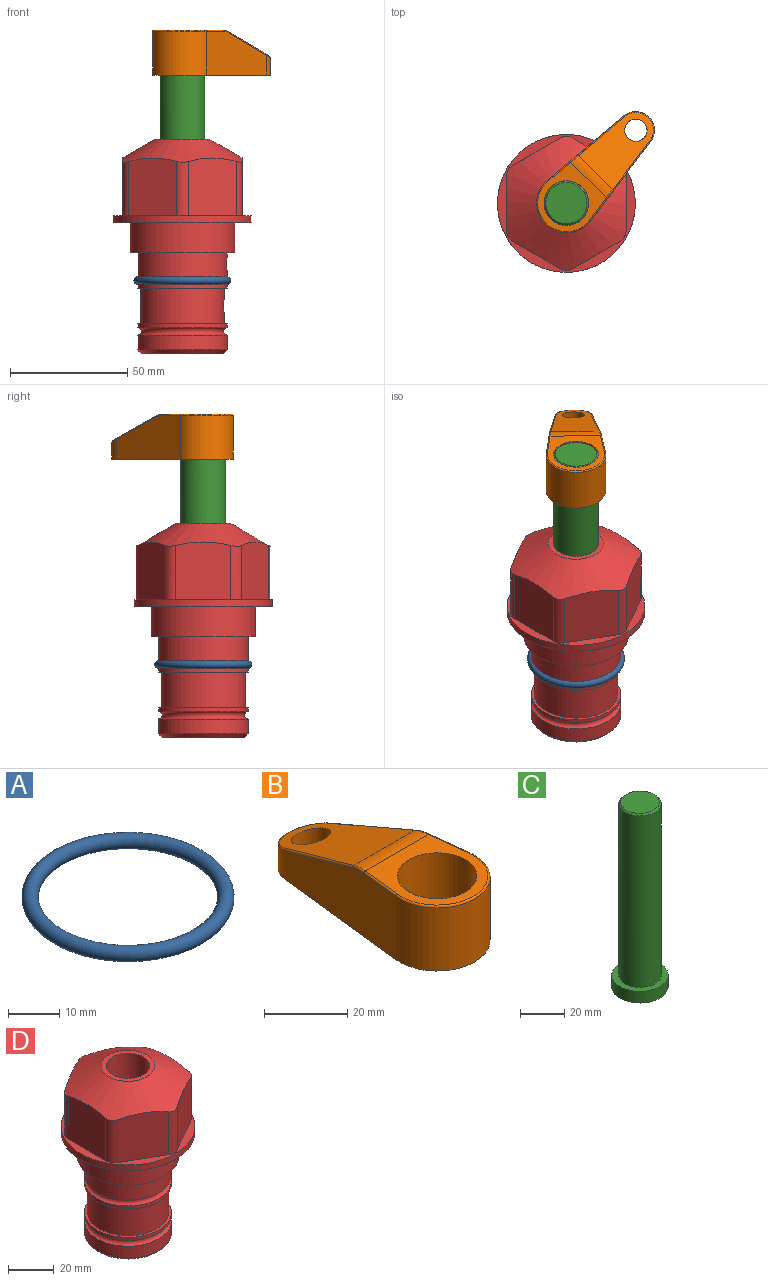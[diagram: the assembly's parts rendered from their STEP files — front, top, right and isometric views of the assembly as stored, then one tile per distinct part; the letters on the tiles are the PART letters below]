
ASSEMBLY  parts=4 mates=2
PART A: 1 faces, bbox 44.7x44.7x3.2 mm
  f0: torus R=19.05mm, axis (0,0,1), area 1193.9mm2
PART B: 44 faces, bbox 27.5x64.5x19.1 mm
  f0: plane 2.3x0.95mm, normal (0,0,-1), area 1mm2, adj f25,f30,f34
  f1: plane 63.5x25.4mm, normal (0,0,-1), area 561.7mm2, adj f2,f3,f4,f5,f6,f7,f19,f20
  f2: cylinder r=12.7mm len=25.4mm, axis (0,0,-1), area 792.2mm2, adj f1,f3,f5,f13
  f3: plane 42.33x18.54mm, normal (0.99,0.11,0), area 647mm2, adj f1,f2,f4,f11,f12,f14
  f4: cylinder r=7.94mm len=15.78mm, axis (0,0,-1), area 158.6mm2, adj f1,f3,f5,f16
  f5: plane 42.33x18.54mm, normal (-0.99,0.11,0), area 647mm2, adj f1,f2,f4,f15,f17,f18
  f6: cylinder r=9.53mm len=19.05mm, axis (0,0,-1), area 1140.1mm2, adj f1,f8
  f7: cylinder r=4.76mm len=10.98mm, axis (0,0,-1), area 276.1mm2, adj f1,f9
  f8: plane 25.83x24.38mm, normal (0,0,1), area 262.2mm2, adj f6,f10,f11,f13,f15
  f9: plane 32.49x20.55mm, normal (0,0.34,0.94), area 489.9mm2, adj f7,f10,f14,f16,f18
  f10: cylinder r=12.7mm len=21.49mm, axis (-1,0,0), area 93.2mm2, adj f8,f9,f12,f17
  f11: cylinder r=0.51mm len=12.34mm, axis (0.11,-0.99,0), area 9.9mm2, adj f3,f8,f12,f13
  f12: bspline ~7.62x1.64mm, area 3.5mm2, adj f3,f10,f11,f14
  f13: torus R=12.19mm, axis (0,0,1), area 33.6mm2, adj f2,f8,f11,f15
  f14: cylinder r=0.51mm len=26.01mm, axis (0.1,-0.93,0.34), area 21.6mm2, adj f3,f9,f12,f16
  f15: cylinder r=0.51mm len=12.34mm, axis (0.11,0.99,0), area 9.9mm2, adj f5,f8,f13,f17
  f16: bspline ~15.78x7.05mm, area 15.7mm2, adj f4,f9,f14,f18
  f17: bspline ~7.62x1.64mm, area 3.5mm2, adj f5,f10,f15,f18
  f18: cylinder r=0.51mm len=26.01mm, axis (0.1,0.93,-0.34), area 21.6mm2, adj f5,f9,f16,f17
  f19: plane 21.6x14.29mm, normal (-0.99,-0.11,0), area 242.6mm2, adj f1,f26,f28,f34,f36,f38
  f20: plane 21.6x14.29mm, normal (0.99,-0.11,0), area 242.6mm2, adj f1,f27,f29,f37,f39,f41
  f21: cylinder r=12.7mm len=14.29mm, axis (0,0,-1), area 173.2mm2, adj f1,f26,f27,f30,f31,f33
  f22: cylinder r=7.94mm len=7.63mm, axis (0,0,-1), area 53.8mm2, adj f1,f28,f29,f42
  f23: plane 2.3x0.95mm, normal (0,0,-1), area 1mm2, adj f25,f33,f37
  f24: plane 17.94x12.32mm, normal (0,-0.34,-0.94), area 191.2mm2, adj f25,f38,f41,f42
  f25: cylinder r=9.53mm len=12.93mm, axis (-1,0,0), area 37.5mm2, adj f0,f23,f24,f31,f36,f39
  f26: cylinder r=1.59mm len=14.29mm, axis (0,0,-1), area 49mm2, adj f1,f19,f21,f32
  f27: cylinder r=1.59mm len=14.29mm, axis (0,0,-1), area 49mm2, adj f1,f20,f21,f35
  f28: cylinder r=1.59mm len=7.28mm, axis (0,0,-1), area 22.1mm2, adj f1,f19,f22,f40
  f29: cylinder r=1.59mm len=7.28mm, axis (0,0,-1), area 22.1mm2, adj f1,f20,f22,f43
  f30: torus R=14.29mm, axis (0,0,1), area 5.8mm2, adj f0,f21,f31,f32
  f31: bspline ~11.06x2.73mm, area 20.8mm2, adj f21,f25,f30,f33
  f32: sphere r=1.59mm, area 5.4mm2, adj f26,f30,f34
  f33: torus R=14.29mm, axis (0,0,1), area 5.8mm2, adj f21,f23,f31,f35
  f34: cylinder r=1.59mm len=1.68mm, axis (-0.11,0.99,0), area 2.4mm2, adj f0,f19,f32,f36
  f35: sphere r=1.59mm, area 5.4mm2, adj f27,f33,f37
  f36: bspline ~5.82x2.33mm, area 7.7mm2, adj f19,f25,f34,f38
  f37: cylinder r=1.59mm len=1.68mm, axis (0.11,0.99,0), area 2.4mm2, adj f20,f23,f35,f39
  f38: cylinder r=1.59mm len=18.33mm, axis (0.1,-0.93,0.34), area 46.7mm2, adj f19,f24,f36,f40
  f39: bspline ~5.82x2.33mm, area 7.7mm2, adj f20,f25,f37,f41
  f40: sphere r=1.59mm, area 3.6mm2, adj f28,f38,f42
  f41: cylinder r=1.59mm len=18.33mm, axis (0.1,0.93,-0.34), area 46.7mm2, adj f20,f24,f39,f43
  f42: bspline ~8.31x1.84mm, area 15.3mm2, adj f22,f24,f40,f43
  f43: sphere r=1.59mm, area 3.6mm2, adj f29,f41,f42
PART C: 6 faces, bbox 25.4x25.4x101.6 mm
  f0: plane 17.46x17.46mm, normal (0,0,1), area 239.5mm2, adj f5
  f1: plane 25.4x25.4mm, normal (0,0,-1), area 506.7mm2, adj f2
  f2: cylinder r=12.7mm len=25.4mm, axis (0,0,1), area 506.7mm2, adj f1,f3
  f3: plane 25.4x25.4mm, normal (0,0,1), area 221.7mm2, adj f2,f4
  f4: cylinder r=9.53mm len=94.46mm, axis (0,0,1), area 5653mm2, adj f3,f5
  f5: cone r=8.73mm half-angle=45deg, axis (0,0,-1), area 64.4mm2, adj f0,f4
PART D: 36 faces, bbox 58.7x58.7x91.2 mm
  f0: cylinder r=17.78mm len=35.56mm, axis (0,0,1), area 1670.8mm2, adj f23,f24,f31
  f1: cylinder r=19.05mm len=38.1mm, axis (0,0,1), area 1191.9mm2, adj f26,f27,f30
  f2: plane 58.66x58.66mm, normal (0,0,-1), area 1150.6mm2, adj f3,f28
  f3: cylinder r=29.33mm len=58.66mm, axis (0,0,-1), area 585.1mm2, adj f2,f4
  f4: plane 58.66x58.66mm, normal (0,0,1), area 475.9mm2, adj f3,f5,f6,f7,f8,f9,f10,f11
  f5: plane 24.5x20.32mm, normal (0.5,-0.87,0), area 562.8mm2, adj f4,f15,f16,f17
  f6: plane 24.5x20.32mm, normal (-0.5,-0.87,0), area 562.8mm2, adj f4,f14,f15,f17
  f7: plane 24.5x23.48mm, normal (-1,0,0), area 562.8mm2, adj f4,f13,f14,f17
  f8: plane 24.5x20.32mm, normal (-0.5,0.87,0), area 562.8mm2, adj f4,f12,f13,f17
  f9: plane 24.5x20.32mm, normal (0.5,0.87,0), area 562.8mm2, adj f4,f11,f12,f17
  f10: plane 24.5x23.48mm, normal (1,0,0), area 562.8mm2, adj f4,f11,f16,f17
  f11: cylinder r=5.08mm len=23.01mm, axis (0,0,-1), area 121.2mm2, adj f4,f9,f10,f17
  f12: cylinder r=5.08mm len=23.01mm, axis (0,0,-1), area 121.2mm2, adj f4,f8,f9,f17
  f13: cylinder r=5.08mm len=23.01mm, axis (0,0,-1), area 121.2mm2, adj f4,f7,f8,f17
  f14: cylinder r=5.08mm len=23.01mm, axis (0,0,-1), area 121.2mm2, adj f4,f6,f7,f17
  f15: cylinder r=5.08mm len=23.01mm, axis (0,0,-1), area 121.2mm2, adj f4,f5,f6,f17
  f16: cylinder r=5.08mm len=23.01mm, axis (0,0,-1), area 121.2mm2, adj f4,f5,f10,f17
  f17: cone r=11.73mm half-angle=60deg, axis (0,0,-1), area 2071.8mm2, adj f5,f6,f7,f8,f9,f10,f11,f12
  f18: plane 23.46x23.46mm, normal (0,0,1), area 147.4mm2, adj f17,f35
  f19: plane 34.93x34.93mm, normal (0,0,-1), area 958mm2, adj f29
  f20: cylinder r=19.05mm len=38.1mm, axis (0,0,1), area 760.1mm2, adj f21,f29
  f21: torus R=19.05mm, axis (0,0,1), area 565.3mm2, adj f20,f22
  f22: cylinder r=19.05mm len=38.1mm, axis (0,0,1), area 190mm2, adj f21,f23
  f23: plane 38.1x38.1mm, normal (0,0,1), area 146.9mm2, adj f0,f22
  f24: plane 38.1x38.1mm, normal (0,0,-1), area 146.9mm2, adj f0,f25
  f25: cylinder r=19.05mm len=38.1mm, axis (0,0,1), area 190mm2, adj f24,f26
  f26: torus R=19.05mm, axis (0,0,1), area 565.3mm2, adj f1,f25
  f27: plane 44.45x44.45mm, normal (0,0,-1), area 411.7mm2, adj f1,f28
  f28: cylinder r=22.23mm len=44.45mm, axis (0,0,1), area 1773.5mm2, adj f2,f27
  f29: cone r=19.05mm half-angle=45deg, axis (0,0,1), area 257.5mm2, adj f19,f20
  f30: cylinder r=3.17mm len=6.75mm, axis (-1,0,0), area 128mm2, adj f1,f33
  f31: cylinder r=3.17mm len=6.35mm, axis (-1,0,0), area 102.5mm2, adj f0,f33
  f32: plane 25.4x25.4mm, normal (0,0,1), area 506.7mm2, adj f33
  f33: cylinder r=12.7mm len=66.42mm, axis (0,0,-1), area 5236.2mm2, adj f30,f31,f32,f34
  f34: cone r=9.53mm half-angle=30deg, axis (0,0,-1), area 443.4mm2, adj f33,f35
  f35: cylinder r=9.53mm len=19.05mm, axis (0,0,-1), area 849mm2, adj f18,f34
PLACE A at identity
PLACE B rot(axis=(0,0,-1),43.6deg) t=(0,0,62.94)mm
PLACE C rot(axis=(0,0,-1),43.6deg) t=(0,0,8.33)mm
PLACE D at identity fixed
MATE cylindrical C.f2 <-> D.f0  axis (0,0,1) through (0,0,33.97)mm
MATE fastened B.f2 <-> C.f2  axis (0,0,-1) through (0,0,81.99)mm
